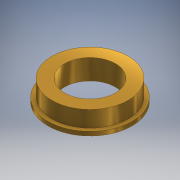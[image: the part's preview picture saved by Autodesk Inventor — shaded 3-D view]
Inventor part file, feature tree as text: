
AUTODESK INVENTOR PART (.ipt)
format: ipt  version: 2016 (Build 200138000, 138)  size: 111,616 bytes
history: native  units: mm
features: extrude x2, other x1, sketch x1
ambient origin geometry x8: Origin, YZ Plane, XZ Plane, XY Plane, X Axis, Y Axis, Z Axis, Center Point
bodies: Body1 (feature_tree)
feature tree (4):
  other  "ソリッド1"
  sketch  "スケッチ1"
  extrude  "押し出し1"  Depth=10.0mm
  extrude  "押し出し2"  Depth=15.0mm
